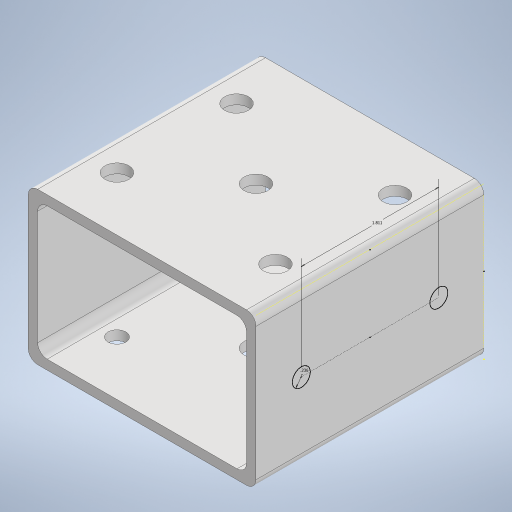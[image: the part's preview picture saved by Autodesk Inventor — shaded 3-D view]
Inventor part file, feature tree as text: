
AUTODESK INVENTOR PART (.ipt)
format: ipt  version: 2023 (Build 270158000, 158)  size: 254,464 bytes
history: native  units: in
note: dims shown in document units (in); Inventor stores cm internally (conversion verified against a paired STEP export)
features: sketch x5, extrude x4, shell x1, fillet x1, projected_geometry x1
ambient origin geometry x8: Origin, YZ Plane, XZ Plane, XY Plane, X Axis, Y Axis, Z Axis, Center Point
bodies: Solid1 (feature_tree)
feature tree (12):
  extrude  "Extrusion1"  Depth=2.0in
  shell  "Shell1"  Thickness=3.0in
  extrude  "Extrusion2"  Depth=0.125in
  extrude  "Extrusion3"  Depth=1.5748in
  fillet  "Fillet1"  Radius=4.0in
  extrude  "Extrusion4"  Depth=4.0in TaperAngle=0.0deg
  sketch  "Sketch5"  dims[d13=0.125in d14=0.315in d15=3.0in d16=0.0in d17=0.2362in d18=1.811in]
  sketch  "Sketch1"  dims[d0=3.0in d1=2.0in d2=3.0in d3=0.0in]
  sketch  "Sketch2"  dims[d4=0.125in d5=0.2362in]
  sketch  "Sketch3"  dims[d6=2.0866in d7=1.5748in d8=4.0in d9=0.0in]
  sketch  "Sketch4"  dims[d10=0.315in d11=4.0in d12=0.0in]
  projected_geometry  "Projected Loop1"
